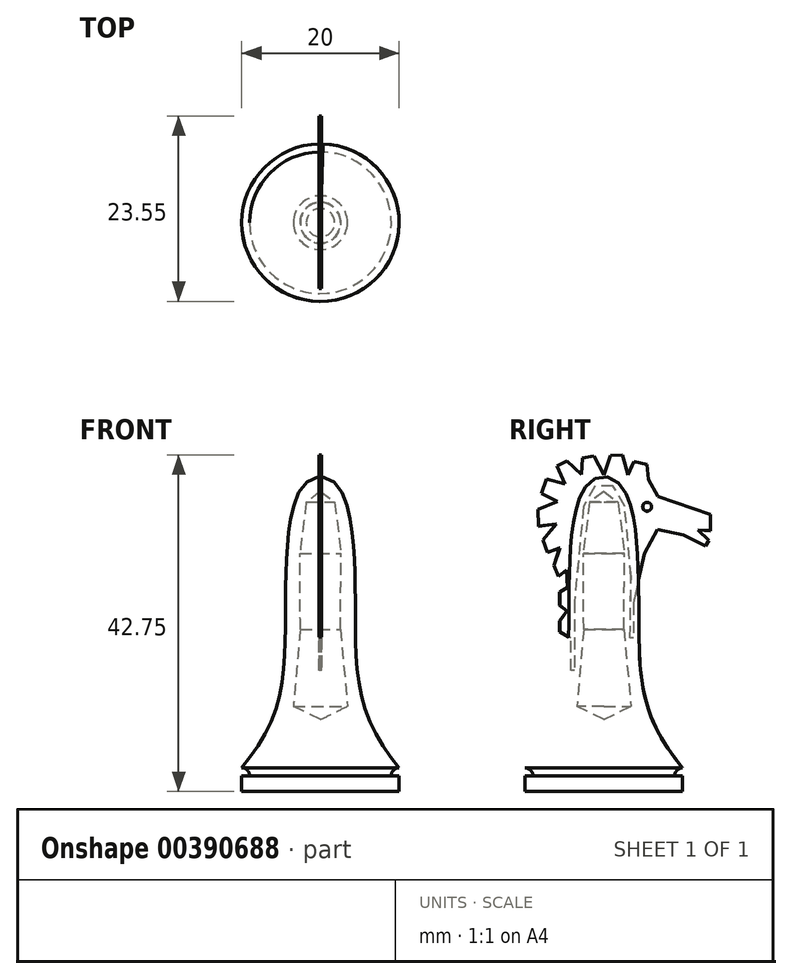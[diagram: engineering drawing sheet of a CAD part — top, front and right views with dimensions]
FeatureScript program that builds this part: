
annotation { "Feature Type Name" : "Feature", "Feature Type Description" : "" }
export const myFeature = defineFeature(function(context is Context, id is Id, definition is map)
    precondition{}
    {
        {
            assignVariable(context, id + "F0", {"name" : "r", "anyValue" : 1});
        }
        {
            var Q0;
            Q0=qCreatedBy(makeId("Front.planeOp"),FACE);
            var sketch = newSketch(context, id + "F1", { "sketchPlane" : qUnion([Q0])});
            skLineSegment(sketch, "E0", {"start": v(0, 0) * mm, "end": v(10, 0) * mm});
            skLineSegment(sketch, "E1", {"start": v(10, 0) * mm, "end": v(10, 2) * mm});
            skLineSegment(sketch, "E2", {"start": v(10, 2) * mm, "end": v(9, 2) * mm});
            skPoint(sketch, "E3.endSnap0", {"position": v(10, 1) * mm});
            skArc(sketch, "E4", {"start": v(9, 2) * mm, "mid": v(9.3, 2.7) * mm, "end": v(10, 3) * mm});
            skFitSpline(sketch, "E5", {"points": [v(10, 3) * mm, v(4.45, 21.57) * mm, v(0, 40) * mm], "startDerivative": vector(-30.93, 37.26) * mm, "endDerivative": vector(-27.95, 0.22) * mm});
            skLineSegment(sketch, "E6", {"start": v(0, 0) * mm, "end": v(0, 40) * mm});
            skLineSegment(sketch, "E7", {"start": v(0, 38.14) * mm, "end": v(1.8, 36.76) * mm});
            skLineSegment(sketch, "E8", {"start": v(1.8, 36.76) * mm, "end": v(2.62, 30.24) * mm});
            skLineSegment(sketch, "E9", {"start": v(2.62, 30.24) * mm, "end": v(2.55, 20.6) * mm});
            skLineSegment(sketch, "E10", {"start": v(2.55, 20.6) * mm, "end": v(3.43, 10.82) * mm});
            skLineSegment(sketch, "E11", {"start": v(3.43, 10.82) * mm, "end": v(0, 9.13) * mm});
            skSolve(sketch);
        }
        {
            var Q0;
            {var subQ0=sQuery(id+"F1.wireOp",EDGE,"E0");Q0=makeQuery(id+"F1.imprint","IMPRINT",FACE,{"disambiguationData":[TD([[makeQuery(id+"F1.imprint","IMPRINT",EDGE,{"derivedFrom":subQ0}),1.0]])]});}
            var Q1;
            {var subQ0=sQuery(id+"F1.wireOp",EDGE,"VEbEkys7-fiXa-1ozb-o1q4-QKgIsQ0NtL7G");Q1=makeQuery(id+"F1.imprint","IMPRINT",FACE,{"disambiguationData":[TD([[makeQuery(id+"F1.imprint","IMPRINT",EDGE,{"derivedFrom":subQ0}),-1.0]])]});}
            var Q2;
            {var subQ0=sQuery(id+"F1.wireOp",EDGE,"E6");var subQ3=sQuery(id+"F1.wireOp",EDGE,"UrGRKQzg-VSOa-ZteD-O5Gp-x69Zk8rxus1x");var subQ5=makeQuery(id+"F1.imprint","INTERSECT",VERTEX,{"derivedFrom":[subQ0,subQ3]});Q2=makeQuery(id+"F1.imprint","IMPRINT",FACE,{"disambiguationData":[TD([[makeQuery(id+"F1.imprint","IMPRINT",EDGE,{"disambiguationData":[TD([[subQ5,-1.0]])],"derivedFrom":subQ3}),1.0]])]});}
            var Q3;
            Q3=sQuery(id+"F1.wireOp",EDGE,"E6");
            revolve(context, id + "F2", {"entities" : qUnion([Q0, Q1, Q2]), "axis" : qUnion([Q3]), "revolveType" : RevolveType.FULL});
        }
        {
            var Q0;
            Q0=qCreatedBy(makeId("Right.planeOp"),FACE);
            var sketch = newSketch(context, id + "F3", { "sketchPlane" : qUnion([Q0])});
            skLineSegment(sketch, "E12", {"start": v(0, 40.2) * mm, "end": v(-1.26, 42.6) * mm});
            skLineSegment(sketch, "E13", {"start": v(-1.26, 42.6) * mm, "end": v(-2.74, 42.38) * mm});
            skLineSegment(sketch, "E14", {"start": v(-2.74, 42.38) * mm, "end": v(-2.83, 40.26) * mm});
            skLineSegment(sketch, "E15", {"start": v(-2.83, 40.26) * mm, "end": v(-4.68, 42.01) * mm});
            skLineSegment(sketch, "E16", {"start": v(-4.68, 42.01) * mm, "end": v(-5.97, 41.37) * mm});
            skLineSegment(sketch, "E17", {"start": v(-5.97, 41.37) * mm, "end": v(-4.96, 39.05) * mm});
            skLineSegment(sketch, "E18", {"start": v(-4.96, 39.05) * mm, "end": v(-7.27, 39.7) * mm});
            skLineSegment(sketch, "E19", {"start": v(-7.27, 39.7) * mm, "end": v(-7.92, 37.85) * mm});
            skLineSegment(sketch, "E20", {"start": v(-7.92, 37.85) * mm, "end": v(-5.88, 36.84) * mm});
            skLineSegment(sketch, "E21", {"start": v(-5.88, 36.84) * mm, "end": v(-8.38, 35.82) * mm});
            skLineSegment(sketch, "E22", {"start": v(-8.38, 35.82) * mm, "end": v(-8.29, 33.7) * mm});
            skLineSegment(sketch, "E23", {"start": v(-8.29, 33.7) * mm, "end": v(-6.07, 33.97) * mm});
            skLineSegment(sketch, "E24", {"start": v(-6.07, 33.97) * mm, "end": v(-7.73, 31.94) * mm});
            skLineSegment(sketch, "E25", {"start": v(-7.73, 31.94) * mm, "end": v(-7.18, 30.37) * mm});
            skLineSegment(sketch, "E26", {"start": v(-7.18, 30.37) * mm, "end": v(-5.6, 30.92) * mm});
            skLineSegment(sketch, "E27", {"start": v(-5.6, 30.92) * mm, "end": v(-6.34, 28.7) * mm});
            skLineSegment(sketch, "E28", {"start": v(-6.34, 28.7) * mm, "end": v(-5.79, 27.32) * mm});
            skLineSegment(sketch, "E29", {"start": v(-5.79, 27.32) * mm, "end": v(-4.74, 28.15) * mm});
            skLineSegment(sketch, "E30", {"start": v(-4.74, 28.15) * mm, "end": v(-4.64, 25.93) * mm});
            skLineSegment(sketch, "E31", {"start": v(-4.64, 25.93) * mm, "end": v(-5.6, 25.37) * mm});
            skLineSegment(sketch, "E32", {"start": v(-5.6, 25.37) * mm, "end": v(-5.6, 23.62) * mm});
            skLineSegment(sketch, "E33", {"start": v(-5.6, 23.62) * mm, "end": v(-4.7, 22.94) * mm});
            skLineSegment(sketch, "E34", {"start": v(-4.7, 22.94) * mm, "end": v(-5.6, 21.68) * mm});
            skLineSegment(sketch, "E35", {"start": v(-5.6, 21.68) * mm, "end": v(-5.6, 20.3) * mm});
            skLineSegment(sketch, "E36", {"start": v(-5.6, 20.3) * mm, "end": v(-4.18, 19.48) * mm});
            skLineSegment(sketch, "E37", {"start": v(0, 40.2) * mm, "end": v(0.87, 42.66) * mm});
            skLineSegment(sketch, "E38", {"start": v(0.87, 42.66) * mm, "end": v(2.34, 42.75) * mm});
            skLineSegment(sketch, "E39", {"start": v(2.34, 42.75) * mm, "end": v(3.08, 40.26) * mm});
            skLineSegment(sketch, "E40", {"start": v(3.08, 40.26) * mm, "end": v(3.82, 41.92) * mm});
            skLineSegment(sketch, "E41", {"start": v(3.82, 41.92) * mm, "end": v(5.49, 41.55) * mm});
            skLineSegment(sketch, "E42", {"start": v(5.49, 41.55) * mm, "end": v(5.67, 39.6) * mm});
            skLineSegment(sketch, "E43", {"start": v(5.67, 39.6) * mm, "end": v(6.87, 37.48) * mm});
            skLineSegment(sketch, "E44", {"start": v(6.87, 37.48) * mm, "end": v(13.53, 35.17) * mm});
            skLineSegment(sketch, "E45", {"start": v(13.53, 35.17) * mm, "end": v(13.55, 33.12) * mm});
            skLineSegment(sketch, "E46", {"start": v(13.55, 33.12) * mm, "end": v(11.98, 33.2) * mm});
            skLineSegment(sketch, "E47", {"start": v(11.98, 33.2) * mm, "end": v(13.37, 31.91) * mm});
            skLineSegment(sketch, "E48", {"start": v(13.37, 31.91) * mm, "end": v(12.9, 31.17) * mm});
            skLineSegment(sketch, "E49", {"start": v(12.9, 31.17) * mm, "end": v(10.13, 32.56) * mm});
            skLineSegment(sketch, "E50", {"start": v(10.13, 32.56) * mm, "end": v(6.8, 33.3) * mm});
            skLineSegment(sketch, "E51", {"start": v(6.8, 33.3) * mm, "end": v(5.14, 30.23) * mm});
            skLineSegment(sketch, "E52", {"start": v(5.14, 30.23) * mm, "end": v(3.77, 23.93) * mm});
            skLineSegment(sketch, "E53", {"start": v(3.77, 23.93) * mm, "end": v(2.65, 36.2) * mm});
            skLineSegment(sketch, "E54", {"start": v(2.65, 36.2) * mm, "end": v(1.18, 38.8) * mm});
            skLineSegment(sketch, "E55", {"start": v(1.18, 38.8) * mm, "end": v(-1.14, 38.8) * mm});
            skLineSegment(sketch, "E56", {"start": v(-1.14, 38.8) * mm, "end": v(-2.57, 36.2) * mm});
            skLineSegment(sketch, "E57", {"start": v(-2.57, 36.2) * mm, "end": v(-4.18, 19.48) * mm});
            skCircle(sketch, "E58", {"center": v(5.5, 36.17) * mm, "radius": 0.56 * mm});
            skLineSegment(sketch, "E59", {"start": v(-4.18, 19.48) * mm, "end": v(-4.18, 15.34) * mm});
            skLineSegment(sketch, "E60", {"start": v(-4.18, 15.34) * mm, "end": v(-3.73, 15.34) * mm});
            skLineSegment(sketch, "E61", {"start": v(-3.73, 15.34) * mm, "end": v(-3.73, 24.15) * mm});
            skLineSegment(sketch, "E62", {"start": v(3.77, 23.93) * mm, "end": v(3.77, 19.52) * mm});
            skLineSegment(sketch, "E63", {"start": v(3.77, 19.52) * mm, "end": v(3.33, 19.52) * mm});
            skLineSegment(sketch, "E64", {"start": v(3.33, 19.52) * mm, "end": v(3.47, 27.22) * mm});
            skSolve(sketch);
        }
        {
            var Q0;
            Q0=qSketchRegion(id+"F3",true);
            extrude(context, id + "F4", {"entities" : qUnion([Q0]), "endBound" : BoundingType.SYMMETRIC, "depth" : (getVariable(context, 'r') * 0.3) * mm, "hasDraft" : true, "draftAngle" : 3 * degree, "draftPullDirection" : true});
        }
        {
            var Q0;
            Q0=makeQuery(id+"F4.opExtrude","SWEPT_BODY",BODY,{"disambiguationData":[OSD([sQuery(id+"F3.wireOp",EDGE,"E12"),sQuery(id+"F3.wireOp",EDGE,"E13"),sQuery(id+"F3.wireOp",EDGE,"E14"),sQuery(id+"F3.wireOp",EDGE,"E15"),sQuery(id+"F3.wireOp",EDGE,"E16"),sQuery(id+"F3.wireOp",EDGE,"E17"),sQuery(id+"F3.wireOp",EDGE,"E18"),sQuery(id+"F3.wireOp",EDGE,"E19"),sQuery(id+"F3.wireOp",EDGE,"E20"),sQuery(id+"F3.wireOp",EDGE,"E21"),sQuery(id+"F3.wireOp",EDGE,"E22"),sQuery(id+"F3.wireOp",EDGE,"E23"),sQuery(id+"F3.wireOp",EDGE,"E24"),sQuery(id+"F3.wireOp",EDGE,"E25"),sQuery(id+"F3.wireOp",EDGE,"E26"),sQuery(id+"F3.wireOp",EDGE,"E27"),sQuery(id+"F3.wireOp",EDGE,"E28"),sQuery(id+"F3.wireOp",EDGE,"E29"),sQuery(id+"F3.wireOp",EDGE,"E30"),sQuery(id+"F3.wireOp",EDGE,"E31"),sQuery(id+"F3.wireOp",EDGE,"E32"),sQuery(id+"F3.wireOp",EDGE,"E33"),sQuery(id+"F3.wireOp",EDGE,"E34"),sQuery(id+"F3.wireOp",EDGE,"E35"),sQuery(id+"F3.wireOp",EDGE,"E36"),sQuery(id+"F3.wireOp",EDGE,"E37"),sQuery(id+"F3.wireOp",EDGE,"E38"),sQuery(id+"F3.wireOp",EDGE,"E39"),sQuery(id+"F3.wireOp",EDGE,"E40"),sQuery(id+"F3.wireOp",EDGE,"E41"),sQuery(id+"F3.wireOp",EDGE,"E42"),sQuery(id+"F3.wireOp",EDGE,"E43"),sQuery(id+"F3.wireOp",EDGE,"E44"),sQuery(id+"F3.wireOp",EDGE,"E45"),sQuery(id+"F3.wireOp",EDGE,"E46"),sQuery(id+"F3.wireOp",EDGE,"E47"),sQuery(id+"F3.wireOp",EDGE,"E48"),sQuery(id+"F3.wireOp",EDGE,"E49"),sQuery(id+"F3.wireOp",EDGE,"E50"),sQuery(id+"F3.wireOp",EDGE,"E51"),sQuery(id+"F3.wireOp",EDGE,"E52"),sQuery(id+"F3.wireOp",EDGE,"E53"),sQuery(id+"F3.wireOp",EDGE,"E54"),sQuery(id+"F3.wireOp",EDGE,"E55"),sQuery(id+"F3.wireOp",EDGE,"E56"),sQuery(id+"F3.wireOp",EDGE,"E57"),sQuery(id+"F3.wireOp",EDGE,"E58")])]});
            var Q1;
            Q1=makeQuery(id+"F2.opRevolve","SWEPT_BODY",BODY,{"disambiguationData":[OSD([sQuery(id+"F1.wireOp",EDGE,"E0"),sQuery(id+"F1.wireOp",EDGE,"E1"),sQuery(id+"F1.wireOp",EDGE,"E2"),sQuery(id+"F1.wireOp",EDGE,"E4"),sQuery(id+"F1.wireOp",EDGE,"E5"),sQuery(id+"F1.wireOp",EDGE,"E6"),sQuery(id+"F1.wireOp",EDGE,"E7"),sQuery(id+"F1.wireOp",EDGE,"E8"),sQuery(id+"F1.wireOp",EDGE,"E9"),sQuery(id+"F1.wireOp",EDGE,"E10"),sQuery(id+"F1.wireOp",EDGE,"E11")])]});
            booleanBodies(context, id + "F5", {"operationType" : BooleanOperationType.SUBTRACTION, "tools" : qUnion([Q0]), "targets" : qUnion([Q1]), "keepTools" : true});
        }
    });
